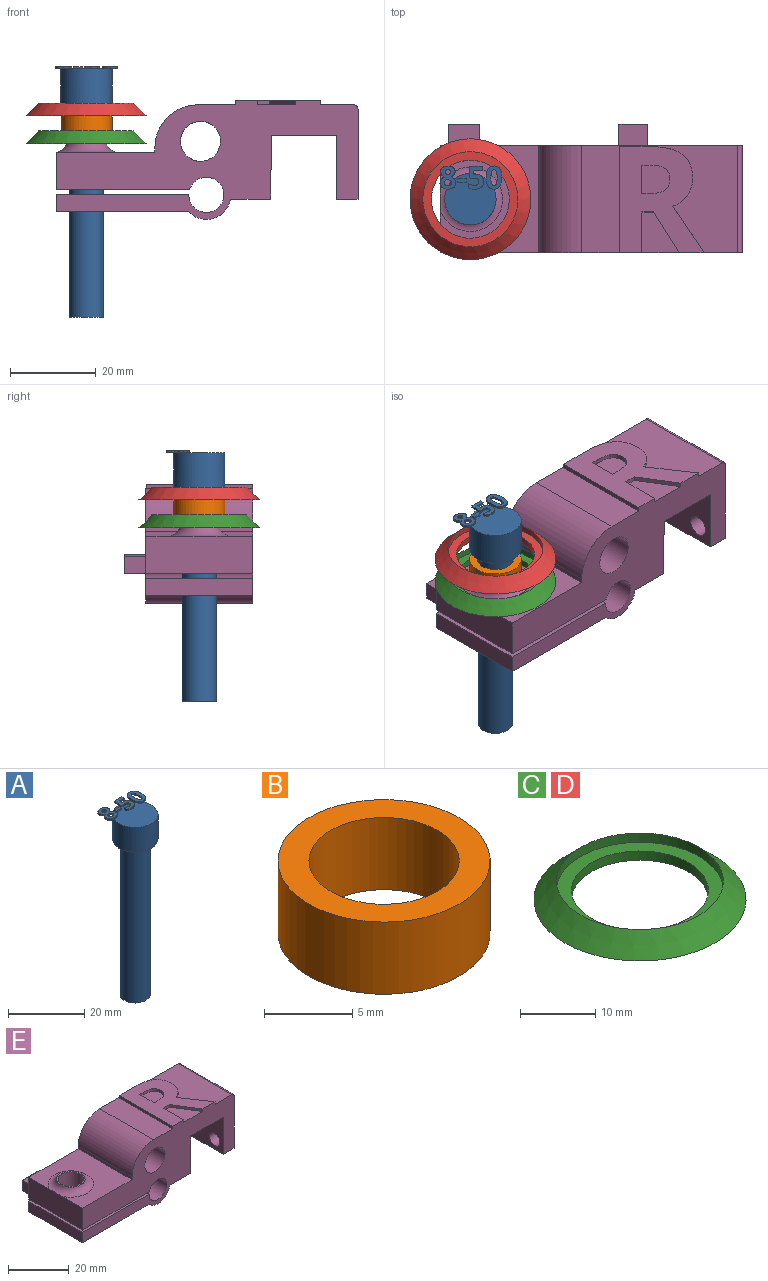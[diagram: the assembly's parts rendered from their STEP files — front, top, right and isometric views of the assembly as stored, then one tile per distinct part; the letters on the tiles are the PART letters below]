
ASSEMBLY  parts=5 mates=4
PART A: 86 faces, bbox 14.5x13.7x58.5 mm
  f0: plane 12x12mm, normal (0,0,1), area 99.4mm2, adj f5,f22,f23,f24,f25,f26,f40,f41
  f1: plane 1x0.26mm, normal (0,0,1), area 0.1mm2, adj f5,f46,f47,f48,f49
  f2: plane 0.85x0.68mm, normal (0,0,1), area 0.2mm2, adj f5,f29,f30,f31
  f3: cylinder r=4mm len=50mm, axis (0,0,-1), area 1256.6mm2, adj f4,f6
  f4: plane 8x8mm, normal (0,0,-1), area 50.3mm2, adj f3
  f5: cylinder r=6mm len=12mm, axis (0,0,-1), area 301.6mm2, adj f0,f1,f2,f6,f39,f45,f67,f85
  f6: plane 12x12mm, normal (0,0,-1), area 62.8mm2, adj f3,f5
  f7: extruded ~0.5x0.46mm, area 0.2mm2, adj f8,f37,f38,f39
  f8: extruded ~0.5x0.46mm, area 0.2mm2, adj f7,f9,f38,f39
  f9: extruded ~0.5x0.39mm, area 0.2mm2, adj f8,f10,f38,f39
  f10: extruded ~0.5x0.4mm, area 0.2mm2, adj f9,f11,f38,f39
  f11: extruded ~0.5x0.49mm, area 0.3mm2, adj f10,f12,f38,f39
  f12: extruded ~0.5x0.5mm, area 0.3mm2, adj f11,f13,f38,f39
  f13: extruded ~0.5x0.39mm, area 0.2mm2, adj f12,f37,f38,f39
  f14: extruded ~1.22x0.5mm, area 0.6mm2, adj f15,f35,f38,f39
  f15: extruded ~1.22x0.5mm, area 0.6mm2, adj f14,f16,f38,f39
  f16: extruded ~0.91x0.5mm, area 0.5mm2, adj f15,f17,f38,f39
  f17: extruded ~0.71x0.5mm, area 0.4mm2, adj f16,f18,f38,f39
  f18: extruded ~0.65x0.61mm, area 0.4mm2, adj f17,f19,f38,f39
  f19: extruded ~0.77x0.62mm, area 0.5mm2, adj f18,f20,f38,f39
  f20: extruded ~0.8x0.5mm, area 0.4mm2, adj f19,f21,f38,f39
  f21: extruded ~1.04x0.5mm, area 0.6mm2, adj f20,f22,f38,f39
  f22: extruded ~1.36x0.5mm, area 0.7mm2, adj f0,f21,f23,f38,f39
  f23: extruded ~1.33x0.5mm, area 0.7mm2, adj f0,f22,f24,f38
  f24: extruded ~1.04x0.51mm, area 0.6mm2, adj f0,f23,f25,f38
  f25: extruded ~0.75x0.5mm, area 0.4mm2, adj f0,f24,f26,f38
  f26: extruded ~0.85x0.66mm, area 0.5mm2, adj f0,f25,f27,f38,f39
  f27: extruded ~0.72x0.56mm, area 0.5mm2, adj f26,f28,f38,f39
  f28: extruded ~0.72x0.5mm, area 0.4mm2, adj f27,f35,f38,f39
  f29: extruded ~0.5x0.45mm, area 0.3mm2, adj f2,f30,f36,f38,f39
  f30: extruded ~0.5x0.47mm, area 0.3mm2, adj f2,f29,f31,f38
  f31: extruded ~0.62x0.5mm, area 0.3mm2, adj f2,f30,f32,f38,f39
  f32: extruded ~0.59x0.5mm, area 0.3mm2, adj f31,f33,f38,f39
  f33: extruded ~0.5x0.48mm, area 0.3mm2, adj f32,f34,f38,f39
  f34: extruded ~0.89x0.77mm, area 0.6mm2, adj f33,f36,f38,f39
  f35: extruded ~0.93x0.5mm, area 0.5mm2, adj f14,f28,f38,f39
  f36: extruded ~0.66x0.5mm, area 0.4mm2, adj f29,f34,f38,f39
  f37: extruded ~0.5x0.39mm, area 0.2mm2, adj f7,f13,f38,f39
  f38: plane 5.4x3.69mm, normal (0,0,1), area 12.7mm2, adj f7,f8,f9,f10,f11,f12,f13,f14
  f39: plane 5.4x3.53mm, normal (0,0,-1), area 10.2mm2, adj f5,f7,f8,f9,f10,f11,f12,f13
  f40: plane 0.9x0.5mm, normal (-1,0,0), area 0.4mm2, adj f0,f41,f43,f44
  f41: plane 1.93x0.5mm, normal (0,-1,0), area 1mm2, adj f0,f40,f42,f44
  f42: plane 0.9x0.5mm, normal (1,0,0), area 0.4mm2, adj f0,f41,f43,f44
  f43: plane 1.93x0.5mm, normal (0,1,0), area 1mm2, adj f0,f40,f42,f44
  f44: plane 1.93x0.9mm, normal (0,0,1), area 1.7mm2, adj f40,f41,f42,f43
  f45: plane 0.76x0.31mm, normal (0,0,-1), area 0mm2, adj f5,f46
  f46: extruded ~1.21x0.5mm, area 0.7mm2, adj f0,f1,f45,f47,f65,f66
  f47: extruded ~0.54x0.5mm, area 0.3mm2, adj f1,f46,f48,f66
  f48: plane 0.5x0.13mm, normal (-0.2,0.98,0), area 0.1mm2, adj f1,f47,f49,f66
  f49: plane 1.03x0.5mm, normal (1,-0.09,0), area 0.5mm2, adj f1,f48,f50,f66,f67
  f50: plane 1.88x0.5mm, normal (0,-1,0), area 0.9mm2, adj f49,f51,f66,f67
  f51: plane 0.94x0.5mm, normal (1,0,0), area 0.5mm2, adj f50,f52,f66,f67
  f52: plane 2.85x0.5mm, normal (0,1,0), area 1.4mm2, adj f51,f53,f66,f67
  f53: plane 2.68x0.5mm, normal (-1,0.07,0), area 1.3mm2, adj f0,f52,f54,f66,f67
  f54: plane 0.5x0.44mm, normal (-0.47,-0.88,0), area 0.3mm2, adj f0,f53,f55,f66
  f55: extruded ~0.5x0.37mm, area 0.2mm2, adj f0,f54,f56,f66
  f56: extruded ~0.5x0.42mm, area 0.2mm2, adj f0,f55,f57,f66
  f57: extruded ~1.05x0.8mm, area 0.8mm2, adj f0,f56,f58,f66
  f58: extruded ~1.02x0.83mm, area 0.8mm2, adj f0,f57,f59,f66
  f59: extruded ~0.72x0.5mm, area 0.4mm2, adj f0,f58,f60,f66
  f60: extruded ~0.66x0.5mm, area 0.4mm2, adj f0,f59,f61,f66
  f61: plane 0.96x0.5mm, normal (-1,0,0), area 0.5mm2, adj f0,f60,f62,f66
  f62: extruded ~1.42x0.5mm, area 0.7mm2, adj f0,f61,f63,f66
  f63: extruded ~1.55x0.5mm, area 0.8mm2, adj f0,f62,f64,f66
  f64: extruded ~1.36x0.54mm, area 0.8mm2, adj f0,f63,f65,f66
  f65: extruded ~1.17x0.5mm, area 0.6mm2, adj f0,f46,f64,f66
  f66: plane 5.33x3.51mm, normal (0,0,1), area 10.9mm2, adj f46,f47,f48,f49,f50,f51,f52,f53
  f67: plane 2.97x1.71mm, normal (0,0,-1), area 3.5mm2, adj f5,f49,f50,f51,f52,f53
  f68: extruded ~1.39x0.5mm, area 0.7mm2, adj f69,f83,f84,f85
  f69: extruded ~1.39x0.5mm, area 0.7mm2, adj f68,f70,f84,f85
  f70: extruded ~0.56x0.5mm, area 0.4mm2, adj f69,f71,f84,f85
  f71: extruded ~0.56x0.5mm, area 0.4mm2, adj f70,f72,f84,f85
  f72: extruded ~1.39x0.5mm, area 0.7mm2, adj f71,f73,f84,f85
  f73: extruded ~1.38x0.5mm, area 0.7mm2, adj f72,f74,f84,f85
  f74: extruded ~0.56x0.5mm, area 0.4mm2, adj f73,f83,f84,f85
  f75: extruded ~2.04x0.5mm, area 1.1mm2, adj f76,f82,f84,f85
  f76: extruded ~2.02x0.5mm, area 1.1mm2, adj f75,f77,f84,f85
  f77: extruded ~1.38x0.69mm, area 0.8mm2, adj f76,f78,f84,f85
  f78: extruded ~1.38x0.66mm, area 0.8mm2, adj f77,f79,f84,f85
  f79: extruded ~2.05x0.5mm, area 1.1mm2, adj f78,f80,f84,f85
  f80: extruded ~2.02x0.5mm, area 1mm2, adj f0,f79,f81,f84,f85
  f81: extruded ~1.37x0.68mm, area 0.8mm2, adj f0,f80,f82,f84
  f82: extruded ~1.39x0.66mm, area 0.8mm2, adj f0,f75,f81,f84,f85
  f83: extruded ~0.56x0.5mm, area 0.4mm2, adj f68,f74,f84,f85
  f84: plane 5.41x3.68mm, normal (0,0,1), area 12.1mm2, adj f68,f69,f70,f71,f72,f73,f74,f75
  f85: plane 5.41x3.68mm, normal (0,0,-1), area 10.3mm2, adj f5,f68,f69,f70,f71,f72,f73,f74
PART B: 4 faces, bbox 12x12x5 mm
  f0: cylinder r=4.25mm len=8.5mm, axis (0,0,-1), area 133.5mm2, adj f2,f3
  f1: cylinder r=6mm len=12mm, axis (0,0,-1), area 188.5mm2, adj f2,f3
  f2: plane 12x12mm, normal (0,0,1), area 56.4mm2, adj f0,f1
  f3: plane 12x12mm, normal (0,0,-1), area 56.4mm2, adj f0,f1
PART C: 5 faces, bbox 28.2x28.2x3 mm
  f0: cone r=11.1mm half-angle=45deg, axis (0,0,-1), area 335.9mm2, adj f1,f4
  f1: cylinder r=11.1mm len=22.2mm, axis (0,0,-1), area 104.6mm2, adj f0,f2
  f2: plane 22.2x22.2mm, normal (0,0,1), area 126.9mm2, adj f1,f3
  f3: cylinder r=9.1mm len=18.2mm, axis (0,0,-1), area 85.8mm2, adj f2,f4
  f4: plane 28.2x28.2mm, normal (0,0,-1), area 364.4mm2, adj f0,f3
PART D: same geometry as C
PART E: 56 faces, bbox 73.9x30x27.7 mm
  f0: plane 36.42x25mm, normal (0,0,1), area 517.1mm2, adj f14,f15,f25,f27,f40,f41,f42,f43
  f1: plane 9.51x8.71mm, normal (0,0,1), area 54.7mm2, adj f14,f37,f38,f39
  f2: plane 25x4.12mm, normal (-1,0,0), area 103mm2, adj f5,f14,f15,f19
  f3: cylinder r=4.17mm len=8.35mm, axis (0,0,1), area 108.1mm2, adj f5,f19
  f4: plane 25x9.34mm, normal (0,0,-1), area 233.4mm2, adj f13,f14,f15,f17
  f5: plane 30.88x25mm, normal (0,0,-1), area 717.2mm2, adj f2,f3,f14,f15,f17
  f6: plane 25x8.82mm, normal (-1,0,0), area 219.6mm2, adj f7,f14,f15,f20,f24
  f7: plane 25x23mm, normal (0,0,1), area 400mm2, adj f6,f8,f14,f15,f24
  f8: plane 25x1.1mm, normal (-1,0,0), area 27.5mm2, adj f7,f14,f15,f25
  f9: plane 25x21.09mm, normal (1,0,0), area 493.5mm2, adj f10,f14,f15,f22,f23,f27
  f10: plane 25x5mm, normal (0,0,-1), area 125mm2, adj f9,f11,f14,f15
  f11: plane 25x15mm, normal (-1,0,0), area 341.3mm2, adj f10,f12,f14,f15,f22,f23
  f12: plane 25x15.2mm, normal (0,0,-1), area 380mm2, adj f11,f13,f14,f15
  f13: plane 25x14.91mm, normal (1,0,-0.01), area 372.8mm2, adj f4,f12,f14,f15
  f14: plane 70.42x27.75mm, normal (0,-1,0), area 1033.3mm2, adj f0,f1,f2,f4,f5,f6,f7,f8
  f15: plane 70.42x26.75mm, normal (0,1,0), area 962.2mm2, adj f0,f2,f4,f5,f6,f7,f8,f9
  f16: cylinder r=4.17mm len=10.78mm, axis (0,0,1), area 282.8mm2, adj f20,f21
  f17: cylinder r=5.75mm len=25mm, axis (0,-1,0), area 315.9mm2, adj f4,f5,f14,f15
  f18: cylinder r=4.1mm len=25mm, axis (0,-1,0), area 618.7mm2, adj f14,f15,f19,f20
  f19: plane 30.91x25mm, normal (0,0,1), area 718.1mm2, adj f2,f3,f14,f15,f18
  f20: plane 31.07x30mm, normal (0,0,-1), area 758.4mm2, adj f6,f14,f15,f16,f18,f29,f30,f31
  f21: plane 9.35x9.35mm, normal (0,0,1), area 13.9mm2, adj f16,f24
  f22: cylinder r=2.43mm len=5mm, axis (1,0,0), area 76.2mm2, adj f9,f11
  f23: cylinder r=2.2mm len=5mm, axis (1,0,0), area 69.1mm2, adj f9,f11
  f24: torus R=7.5mm, axis (0,0,-1), area 134.6mm2, adj f6,f7,f21
  f25: cylinder r=10mm len=25mm, axis (0,-1,0), area 392.7mm2, adj f0,f8,f14,f15
  f26: cylinder r=4.68mm len=25mm, axis (0,-1,0), area 735.2mm2, adj f14,f15
  f27: cylinder r=1mm len=25mm, axis (0,-1,0), area 39.3mm2, adj f0,f9,f14,f15
  f28: plane 7.3x5mm, normal (0,0,1), area 36.5mm2, adj f15,f29,f30,f31
  f29: plane 5x4.12mm, normal (-1,0,0), area 20.6mm2, adj f15,f20,f28,f31
  f30: plane 5x4.12mm, normal (1,0,0), area 20.6mm2, adj f15,f20,f28,f31
  f31: plane 7.3x4.12mm, normal (0,1,0), area 30.1mm2, adj f20,f28,f29,f30
  f32: plane 6.63x5mm, normal (0,0,1), area 33.2mm2, adj f15,f33,f35,f36
  f33: plane 5x4.5mm, normal (-1,0,0), area 22.5mm2, adj f15,f32,f34,f36
  f34: plane 6.63x5mm, normal (0,0,-1), area 33.2mm2, adj f15,f33,f35,f36
  f35: plane 5x4.5mm, normal (1,0,0), area 22.5mm2, adj f15,f32,f34,f36
  f36: plane 6.63x4.5mm, normal (0,1,0), area 29.9mm2, adj f32,f33,f34,f35
  f37: plane 9.51x1mm, normal (1,0,0), area 9.5mm2, adj f1,f14,f38,f54
  f38: plane 2.79x1mm, normal (0,-1,0), area 2.8mm2, adj f1,f37,f39,f54
  f39: plane 9.51x5.92mm, normal (-0.85,-0.53,0), area 11.2mm2, adj f1,f14,f38,f54
  f40: extruded ~10.8x7.29mm, area 13mm2, adj f0,f14,f41,f54
  f41: extruded ~3.41x2.67mm, area 4.4mm2, adj f0,f40,f42,f54
  f42: extruded ~3.89x1.2mm, area 4.1mm2, adj f0,f41,f43,f54
  f43: extruded ~5.59x2.42mm, area 6.3mm2, adj f0,f42,f44,f54
  f44: extruded ~7.48x1.84mm, area 7.8mm2, adj f0,f43,f45,f54
  f45: plane 7.22x1mm, normal (0,1,0), area 7.2mm2, adj f0,f44,f46,f54
  f46: plane 24.79x1mm, normal (-1,0,0), area 24.8mm2, adj f0,f14,f45,f54
  f47: plane 1.69x1mm, normal (0,1,0), area 1.7mm2, adj f48,f53,f54,f55
  f48: plane 6.7x1mm, normal (1,0,0), area 6.7mm2, adj f47,f49,f54,f55
  f49: plane 1.6x1mm, normal (0,-1,0), area 1.6mm2, adj f48,f50,f54,f55
  f50: extruded ~3.75x1mm, area 3.9mm2, adj f49,f51,f54,f55
  f51: extruded ~2.51x1.21mm, area 2.9mm2, adj f50,f52,f54,f55
  f52: extruded ~2.61x1.19mm, area 3mm2, adj f51,f53,f54,f55
  f53: extruded ~3.68x1mm, area 3.8mm2, adj f47,f52,f54,f55
  f54: plane 24.79x19.8mm, normal (0,0,1), area 300mm2, adj f14,f37,f38,f39,f40,f41,f42,f43
  f55: plane 6.7x6.56mm, normal (0,0,1), area 38.8mm2, adj f47,f48,f49,f50,f51,f52,f53
PLACE A t=(-103.78,-12.5,-28.71)mm
PLACE B rot(axis=(1,0,0),180deg) t=(-103.78,-12.5,18.29)mm
PLACE C t=(-103.78,-12.5,18.1)mm
PLACE D t=(-103.78,-12.5,24.6)mm
PLACE E t=(0,0,-1.11)mm
MATE fastened A.f3 <-> D.f0  axis (0,0,-1) through (-103.78,-12.5,21.29)mm
MATE fastened B.f0 <-> C.f0  axis (0,0,1) through (-103.78,-12.5,13.29)mm
MATE fastened C.f0 <-> E.f3  axis (0,0,-1) through (-103.78,-12.5,11.79)mm
MATE fastened D.f0 <-> B.f0  axis (0,0,-1) through (-103.78,-12.5,18.29)mm
